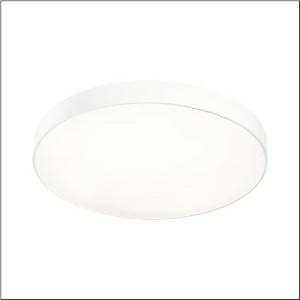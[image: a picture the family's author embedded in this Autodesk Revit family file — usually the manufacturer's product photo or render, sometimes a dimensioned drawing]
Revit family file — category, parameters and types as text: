
# Revit family: round_21_l_51mr38fd0321w
name_source: partatom
category: Lighting Fixtures
units: mm (PartAtom-declared; Revit-internal decimal feet)

## family parameters
Cut with Voids When Loaded = No
Host = Face
Light Source = No
Part Type = Normal
Room Calculation Point = No
Round Connector Dimension = Use Diameter
Shared = No

## types (1)
- Round 21 L (1 x LED, 13590 lm, 97 W, 3000K)
    Apparent Load = 97 VA
    CIE Flux Codes = 49 80 96 100 100
    Color Rendering = 80
    Color Temperature = 3000K
    Default Elevation = 1800 mm
    Description = Round 21 L, wall and ceiling luminaire, primary optical cover: cover, of PMMA, opal, light emission: direct distribution, primary light characteristic: symmetric, installation type: suspended mounting, surface-mounted, LED, rated luminous flux: 13.590lm, luminous efficacy: 140lm/W, light colour: 830, colour temperature: 3000K, control gear: DALI 2, with terminal, 5-pole, mains connection: 230V, AC, 50/60Hz, rated input power: 97W, housing, of aluminium, coated, white, diameter: 850mm, height: 62mm, protection rating (complete): IP40, insulation class (complete): insulation class I (protective earthing), certification: CE, impact resistance: IK04, permissible operating ambient temperature: -10..+35°C, packaging unit: 1 piece
    Height = 87 mm
    Lamp = 1 x LED
    Lamp Light Flux = 13590 lm
    Lamp Power = 97 W
    Lamp count = 1
    Length = 850 mm
    Luminous efficacy = 140 lm/W
    Manufacturer = Siteco
    ModVariant = No
    Model = 51MR38FD0321W
    Mounting Place = Ceiling
    Mounting Type = Surface mounted
    Number of Poles = 1
    OnlyDefault = Yes
    Power Factor = 1
    Product Name = Round 21 L
    Product group = wall and ceiling luminaire | ceiling mounted
    ProductGroupID = 305
    Protection Class = Protection class I
    Protection Degree = IP 40
    RLX_Detail_Level = 1
    RLX_Emergency_Light_Flux = 0 lm
    RLX_Emergency_Type = 0
    RLX_Emergency_Type_DB = No
    RlxData = <blob elided: 15017 chars, md5=70aa1940>
    Socket = socket
    Standby Power = 0 W
    System Light Flux = 13590 lm
    System Power = 97 W
    Type Comments = Product without accessories
    Type Image = l_1258320.jpg
    URL = http://relux.com
    VarID = ---
    Voltage = 0 V
    Weight = 0.00 kg
    Width = 0 mm  [stored 0 ft]

note: [stored X ft] marks values corroborated as IEEE doubles in the binary element streams (Revit-internal decimal feet)

## geometry (parser evidence)
native form markers: Sweep x11
no freeform markers — native parametric forms only
